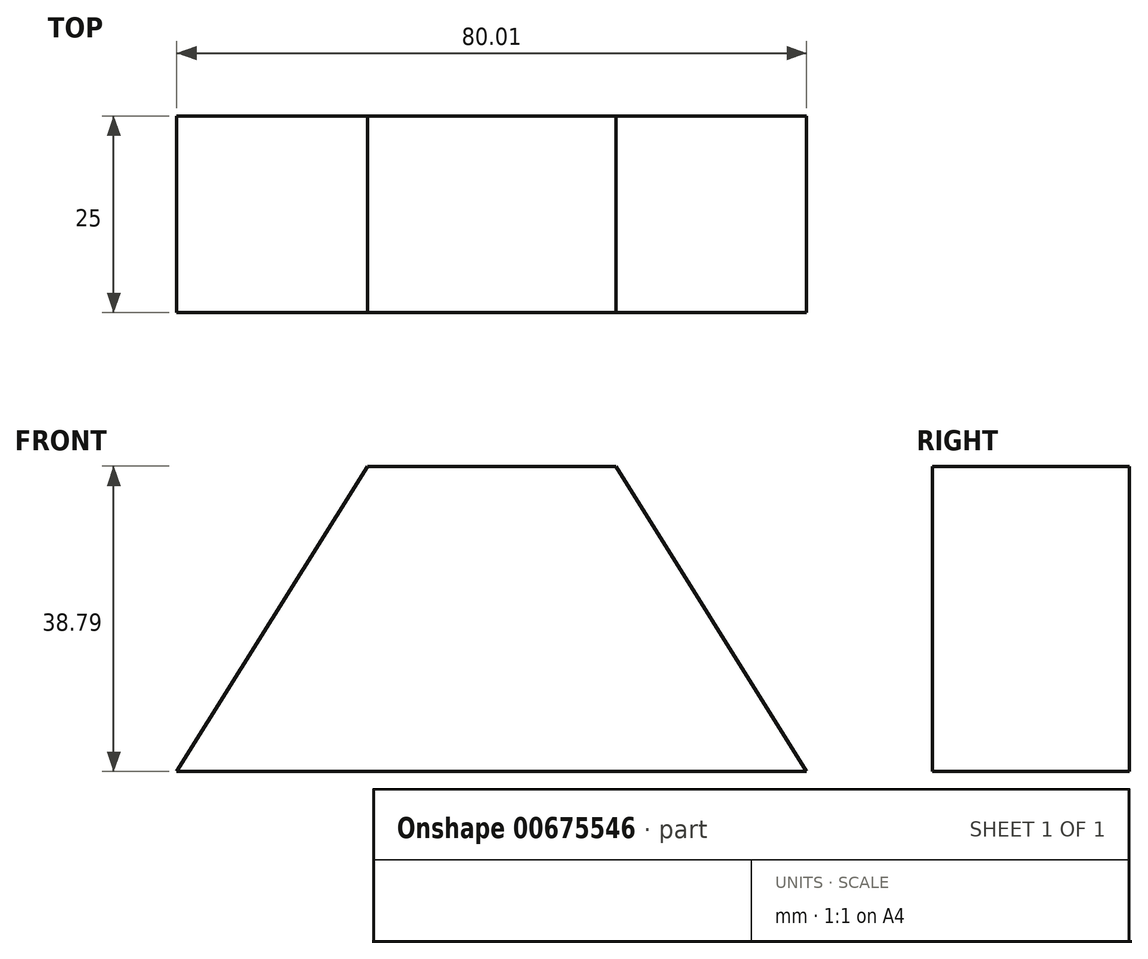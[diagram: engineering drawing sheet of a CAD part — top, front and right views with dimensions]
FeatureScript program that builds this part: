
annotation { "Feature Type Name" : "Feature", "Feature Type Description" : "" }
export const myFeature = defineFeature(function(context is Context, id is Id, definition is map)
    precondition{}
    {
        {
            var Q0;
            Q0=qCreatedBy(makeId("Front.planeOp"),FACE);
            var sketch = newSketch(context, id + "F0", { "sketchPlane" : qUnion([Q0])});
            skLineSegment(sketch, "E0", {"start": v(-21.15, -2.73) * mm, "end": v(58.86, -2.73) * mm});
            skLineSegment(sketch, "E1", {"start": v(58.86, -2.73) * mm, "end": v(34.62, 36.06) * mm});
            skLineSegment(sketch, "E2", {"start": v(34.62, 36.06) * mm, "end": v(3.09, 36.06) * mm});
            skLineSegment(sketch, "E3", {"start": v(-21.15, -2.73) * mm, "end": v(3.09, 36.06) * mm});
            skSolve(sketch);
        }
        {
            var Q0;
            Q0 = qSketchRegion(id + "F0", true);
            extrude(context, id + "F1", {"entities" : qUnion([Q0]), "depth" : 25 * mm, "offsetDistance" : 25 * mm});
        }
    });
